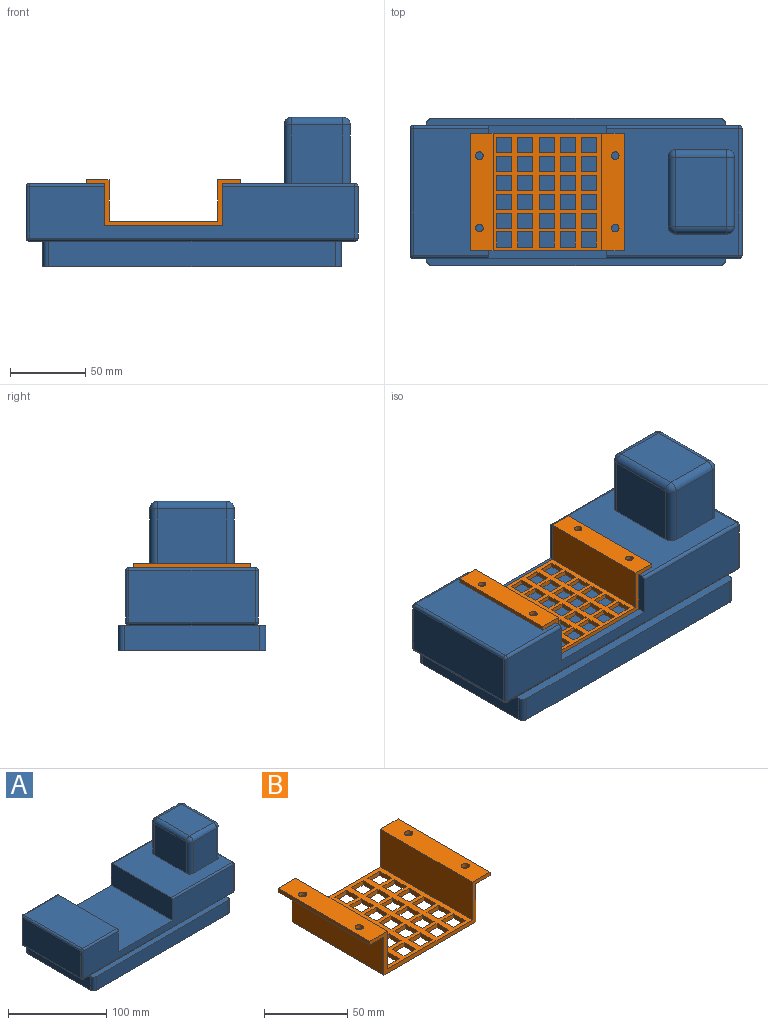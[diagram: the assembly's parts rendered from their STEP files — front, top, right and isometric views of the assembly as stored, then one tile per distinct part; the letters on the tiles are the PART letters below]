
ASSEMBLY  parts=2 mates=1
PART A: 61 faces, bbox 220x98x99 mm
  f0: plane 198x7mm, normal (0,0,1), area 1379.1mm2, adj f2,f3,f4,f7,f8,f37
  f1: plane 198x7mm, normal (0,0,1), area 1379.1mm2, adj f2,f4,f5,f9,f10,f29
  f2: plane 90x17mm, normal (-1,0,0), area 1530mm2, adj f0,f1,f6,f7,f10,f11
  f3: plane 190x17mm, normal (0,-1,0), area 3230mm2, adj f0,f6,f7,f8
  f4: plane 90x17mm, normal (1,0,0), area 1530mm2, adj f0,f1,f6,f8,f9,f18
  f5: plane 190x17mm, normal (0,1,0), area 3230mm2, adj f1,f6,f9,f10
  f6: plane 198x98mm, normal (0,0,-1), area 19390.3mm2, adj f2,f3,f4,f5,f7,f8,f9,f10
  f7: cylinder r=4mm len=17mm, axis (0,0,-1), area 106.8mm2, adj f0,f2,f3,f6
  f8: cylinder r=4mm len=17mm, axis (0,0,1), area 106.8mm2, adj f0,f3,f4,f6
  f9: cylinder r=4mm len=17mm, axis (0,0,-1), area 106.8mm2, adj f1,f4,f5,f6
  f10: cylinder r=4mm len=17mm, axis (0,0,1), area 106.8mm2, adj f1,f2,f5,f6
  f11: plane 84x9mm, normal (0,0,-1), area 756mm2, adj f2,f29,f30,f37
  f12: plane 88x84mm, normal (0,0,1), area 4949.5mm2, adj f19,f34,f40,f43,f44,f45,f46,f47
  f13: plane 216x34mm, normal (0,-1,0), area 5316mm2, adj f19,f20,f21,f26,f31,f37,f41,f43
  f14: plane 216x34mm, normal (0,1,0), area 5316mm2, adj f19,f20,f21,f22,f24,f29,f34,f35
  f15: plane 84x34mm, normal (-1,0,0), area 2856mm2, adj f24,f25,f30,f31
  f16: plane 84x34mm, normal (1,0,0), area 2856mm2, adj f35,f36,f40,f41
  f17: plane 84x50mm, normal (0,0,1), area 4200mm2, adj f20,f22,f25,f26
  f18: plane 84x9mm, normal (0,0,-1), area 756mm2, adj f4,f29,f36,f37
  f19: plane 88x28mm, normal (-1,0,0), area 2462.3mm2, adj f12,f13,f14,f21,f34,f43
  f20: plane 88x28mm, normal (1,0,0), area 2462.3mm2, adj f13,f14,f17,f21,f22,f26
  f21: plane 88x78mm, normal (0,0,1), area 6864mm2, adj f13,f14,f19,f20
  f22: cylinder r=2mm len=50mm, axis (1,0,0), area 157.1mm2, adj f14,f17,f20,f23
  f23: sphere r=2mm, area 6.3mm2, adj f22,f24,f25
  f24: cylinder r=2mm len=34mm, axis (0,0,1), area 106.8mm2, adj f14,f15,f23,f27
  f25: cylinder r=2mm len=84mm, axis (0,1,0), area 263.9mm2, adj f15,f17,f23,f28
  f26: cylinder r=2mm len=50mm, axis (-1,0,0), area 157.1mm2, adj f13,f17,f20,f28
  f27: sphere r=2mm, area 6.3mm2, adj f24,f29,f30
  f28: sphere r=2mm, area 6.3mm2, adj f25,f26,f31
  f29: cylinder r=2mm len=216mm, axis (-1,0,0), area 678.6mm2, adj f1,f11,f14,f18,f27,f32
  f30: cylinder r=2mm len=84mm, axis (0,-1,0), area 263.9mm2, adj f11,f15,f27,f33
  f31: cylinder r=2mm len=34mm, axis (0,0,-1), area 106.8mm2, adj f13,f15,f28,f33
  f32: sphere r=2mm, area 6.3mm2, adj f29,f35,f36
  f33: sphere r=2mm, area 6.3mm2, adj f30,f31,f37
  f34: cylinder r=2mm len=88mm, axis (1,0,0), area 276.5mm2, adj f12,f14,f19,f38
  f35: cylinder r=2mm len=34mm, axis (0,0,-1), area 106.8mm2, adj f14,f16,f32,f38
  f36: cylinder r=2mm len=84mm, axis (0,1,0), area 263.9mm2, adj f16,f18,f32,f39
  f37: cylinder r=2mm len=216mm, axis (1,0,0), area 678.6mm2, adj f0,f11,f13,f18,f33,f39
  f38: sphere r=2mm, area 6.3mm2, adj f34,f35,f40
  f39: sphere r=2mm, area 6.3mm2, adj f36,f37,f41
  f40: cylinder r=2mm len=84mm, axis (0,-1,0), area 263.9mm2, adj f12,f16,f38,f42
  f41: cylinder r=2mm len=34mm, axis (0,0,1), area 106.8mm2, adj f13,f16,f39,f42
  f42: sphere r=2mm, area 6.3mm2, adj f40,f41,f43
  f43: cylinder r=2mm len=88mm, axis (-1,0,0), area 276.5mm2, adj f12,f13,f19,f42
  f44: plane 39x34mm, normal (0,-1,0), area 1326mm2, adj f12,f51,f57,f60
  f45: plane 46x39mm, normal (1,0,0), area 1794mm2, adj f12,f54,f58,f60
  f46: plane 39x34mm, normal (0,1,0), area 1326mm2, adj f12,f49,f53,f54
  f47: plane 46x39mm, normal (-1,0,0), area 1794mm2, adj f12,f49,f51,f52
  f48: plane 46x34mm, normal (0,0,1), area 1564mm2, adj f52,f53,f57,f58
  f49: cylinder r=5mm len=39mm, axis (0,0,-1), area 306.3mm2, adj f12,f46,f47,f50
  f50: sphere r=5mm, area 39.3mm2, adj f49,f52,f53
  f51: cylinder r=5mm len=39mm, axis (0,0,1), area 306.3mm2, adj f12,f44,f47,f55
  f52: cylinder r=5mm len=46mm, axis (0,1,0), area 361.3mm2, adj f47,f48,f50,f55
  f53: cylinder r=5mm len=34mm, axis (1,0,0), area 267mm2, adj f46,f48,f50,f56
  f54: cylinder r=5mm len=39mm, axis (0,0,1), area 306.3mm2, adj f12,f45,f46,f56
  f55: sphere r=5mm, area 39.3mm2, adj f51,f52,f57
  f56: sphere r=5mm, area 39.3mm2, adj f53,f54,f58
  f57: cylinder r=5mm len=34mm, axis (-1,0,0), area 267mm2, adj f44,f48,f55,f59
  f58: cylinder r=5mm len=46mm, axis (0,-1,0), area 361.3mm2, adj f45,f48,f56,f59
  f59: sphere r=5mm, area 39.3mm2, adj f57,f58,f60
  f60: cylinder r=5mm len=39mm, axis (0,0,-1), area 306.3mm2, adj f12,f44,f45,f59
PART B: 138 faces, bbox 102x78x30.7 mm
  f0: plane 78x27.75mm, normal (-1,0,0), area 2164.4mm2, adj f1,f11,f12,f13
  f1: plane 78x72mm, normal (0,0,1), area 2615.8mm2, adj f0,f2,f12,f13,f18,f19,f20,f21
  f2: plane 78x27.75mm, normal (1,0,0), area 2164.4mm2, adj f1,f3,f12,f13
  f3: plane 78x15mm, normal (0,0,1), area 1130.7mm2, adj f2,f4,f12,f13,f16,f17
  f4: plane 78x2.75mm, normal (-1,0,0), area 214.4mm2, adj f3,f5,f12,f13
  f5: plane 78x12mm, normal (0,0,-1), area 896.6mm2, adj f4,f6,f12,f13,f16,f17
  f6: plane 78x28mm, normal (-1,0,0), area 2184mm2, adj f5,f7,f12,f13
  f7: plane 78x78mm, normal (0,0,-1), area 3084mm2, adj f6,f8,f12,f13,f18,f19,f20,f21
  f8: plane 78x28mm, normal (1,0,0), area 2184mm2, adj f7,f9,f12,f13
  f9: plane 78x12mm, normal (0,0,-1), area 896.6mm2, adj f8,f10,f12,f13,f14,f15
  f10: plane 78x2.75mm, normal (1,0,0), area 214.4mm2, adj f9,f11,f12,f13
  f11: plane 78x15mm, normal (0,0,1), area 1130.7mm2, adj f0,f10,f12,f13,f14,f15
  f12: plane 102x30.75mm, normal (0,-1,0), area 466.5mm2, adj f0,f1,f2,f3,f4,f5,f6,f7
  f13: plane 102x30.75mm, normal (0,1,0), area 466.5mm2, adj f0,f1,f2,f3,f4,f5,f6,f7
  f14: cylinder r=2.5mm len=5mm, axis (0,0,1), area 43.2mm2, adj f9,f11
  f15: cylinder r=2.5mm len=5mm, axis (0,0,1), area 43.2mm2, adj f9,f11
  f16: cylinder r=2.5mm len=5mm, axis (0,0,1), area 43.2mm2, adj f3,f5
  f17: cylinder r=2.5mm len=5mm, axis (0,0,1), area 43.2mm2, adj f3,f5
  f18: plane 10x3mm, normal (0,-1,0), area 30mm2, adj f1,f7,f19,f20
  f19: plane 10x3mm, normal (1,0,0), area 30mm2, adj f1,f7,f18,f21
  f20: plane 10x3mm, normal (-1,0,0), area 30mm2, adj f1,f7,f18,f21
  f21: plane 10x3mm, normal (0,1,0), area 30mm2, adj f1,f7,f19,f20
  f22: plane 10x3mm, normal (1,0,0), area 30mm2, adj f1,f7,f23,f24
  f23: plane 10x3mm, normal (0,1,0), area 30mm2, adj f1,f7,f22,f25
  f24: plane 10x3mm, normal (0,-1,0), area 30mm2, adj f1,f7,f22,f25
  f25: plane 10x3mm, normal (-1,0,0), area 30mm2, adj f1,f7,f23,f24
  f26: plane 10x3mm, normal (1,0,0), area 30mm2, adj f1,f7,f27,f28
  f27: plane 10x3mm, normal (0,1,0), area 30mm2, adj f1,f7,f26,f29
  f28: plane 10x3mm, normal (0,-1,0), area 30mm2, adj f1,f7,f26,f29
  f29: plane 10x3mm, normal (-1,0,0), area 30mm2, adj f1,f7,f27,f28
  f30: plane 10x3mm, normal (1,0,0), area 30mm2, adj f1,f7,f31,f32
  f31: plane 10x3mm, normal (0,1,0), area 30mm2, adj f1,f7,f30,f33
  f32: plane 10x3mm, normal (0,-1,0), area 30mm2, adj f1,f7,f30,f33
  f33: plane 10x3mm, normal (-1,0,0), area 30mm2, adj f1,f7,f31,f32
  f34: plane 10x3mm, normal (0,-1,0), area 30mm2, adj f1,f7,f35,f36
  f35: plane 10x3mm, normal (1,0,0), area 30mm2, adj f1,f7,f34,f37
  f36: plane 10x3mm, normal (-1,0,0), area 30mm2, adj f1,f7,f34,f37
  f37: plane 10x3mm, normal (0,1,0), area 30mm2, adj f1,f7,f35,f36
  f38: plane 10x3mm, normal (0,-1,0), area 30mm2, adj f1,f7,f39,f40
  f39: plane 10x3mm, normal (1,0,0), area 30mm2, adj f1,f7,f38,f41
  f40: plane 10x3mm, normal (-1,0,0), area 30mm2, adj f1,f7,f38,f41
  f41: plane 10x3mm, normal (0,1,0), area 30mm2, adj f1,f7,f39,f40
  f42: plane 10x3mm, normal (1,0,0), area 30mm2, adj f1,f7,f43,f44
  f43: plane 10x3mm, normal (0,1,0), area 30mm2, adj f1,f7,f42,f45
  f44: plane 10x3mm, normal (0,-1,0), area 30mm2, adj f1,f7,f42,f45
  f45: plane 10x3mm, normal (-1,0,0), area 30mm2, adj f1,f7,f43,f44
  f46: plane 10x3mm, normal (0,-1,0), area 30mm2, adj f1,f7,f47,f48
  f47: plane 10x3mm, normal (1,0,0), area 30mm2, adj f1,f7,f46,f49
  f48: plane 10x3mm, normal (-1,0,0), area 30mm2, adj f1,f7,f46,f49
  f49: plane 10x3mm, normal (0,1,0), area 30mm2, adj f1,f7,f47,f48
  f50: plane 10x3mm, normal (0,-1,0), area 30mm2, adj f1,f7,f51,f52
  f51: plane 10x3mm, normal (1,0,0), area 30mm2, adj f1,f7,f50,f53
  f52: plane 10x3mm, normal (-1,0,0), area 30mm2, adj f1,f7,f50,f53
  f53: plane 10x3mm, normal (0,1,0), area 30mm2, adj f1,f7,f51,f52
  f54: plane 10x3mm, normal (1,0,0), area 30mm2, adj f1,f7,f55,f56
  f55: plane 10x3mm, normal (0,1,0), area 30mm2, adj f1,f7,f54,f57
  f56: plane 10x3mm, normal (0,-1,0), area 30mm2, adj f1,f7,f54,f57
  f57: plane 10x3mm, normal (-1,0,0), area 30mm2, adj f1,f7,f55,f56
  f58: plane 10x3mm, normal (0,-1,0), area 30mm2, adj f1,f7,f59,f60
  f59: plane 10x3mm, normal (1,0,0), area 30mm2, adj f1,f7,f58,f61
  f60: plane 10x3mm, normal (-1,0,0), area 30mm2, adj f1,f7,f58,f61
  f61: plane 10x3mm, normal (0,1,0), area 30mm2, adj f1,f7,f59,f60
  f62: plane 10x3mm, normal (0,-1,0), area 30mm2, adj f1,f7,f63,f64
  f63: plane 10x3mm, normal (1,0,0), area 30mm2, adj f1,f7,f62,f65
  f64: plane 10x3mm, normal (-1,0,0), area 30mm2, adj f1,f7,f62,f65
  f65: plane 10x3mm, normal (0,1,0), area 30mm2, adj f1,f7,f63,f64
  f66: plane 10x3mm, normal (1,0,0), area 30mm2, adj f1,f7,f67,f68
  f67: plane 10x3mm, normal (0,1,0), area 30mm2, adj f1,f7,f66,f69
  f68: plane 10x3mm, normal (0,-1,0), area 30mm2, adj f1,f7,f66,f69
  f69: plane 10x3mm, normal (-1,0,0), area 30mm2, adj f1,f7,f67,f68
  f70: plane 10x3mm, normal (1,0,0), area 30mm2, adj f1,f7,f71,f72
  f71: plane 10x3mm, normal (0,1,0), area 30mm2, adj f1,f7,f70,f73
  f72: plane 10x3mm, normal (0,-1,0), area 30mm2, adj f1,f7,f70,f73
  f73: plane 10x3mm, normal (-1,0,0), area 30mm2, adj f1,f7,f71,f72
  f74: plane 10x3mm, normal (0,-1,0), area 30mm2, adj f1,f7,f75,f76
  f75: plane 10x3mm, normal (1,0,0), area 30mm2, adj f1,f7,f74,f77
  f76: plane 10x3mm, normal (-1,0,0), area 30mm2, adj f1,f7,f74,f77
  f77: plane 10x3mm, normal (0,1,0), area 30mm2, adj f1,f7,f75,f76
  f78: plane 10x3mm, normal (0,-1,0), area 30mm2, adj f1,f7,f79,f80
  f79: plane 10x3mm, normal (1,0,0), area 30mm2, adj f1,f7,f78,f81
  f80: plane 10x3mm, normal (-1,0,0), area 30mm2, adj f1,f7,f78,f81
  f81: plane 10x3mm, normal (0,1,0), area 30mm2, adj f1,f7,f79,f80
  f82: plane 10x3mm, normal (0,-1,0), area 30mm2, adj f1,f7,f83,f84
  f83: plane 10x3mm, normal (1,0,0), area 30mm2, adj f1,f7,f82,f85
  f84: plane 10x3mm, normal (-1,0,0), area 30mm2, adj f1,f7,f82,f85
  f85: plane 10x3mm, normal (0,1,0), area 30mm2, adj f1,f7,f83,f84
  f86: plane 10x3mm, normal (0,-1,0), area 30mm2, adj f1,f7,f87,f88
  f87: plane 10x3mm, normal (1,0,0), area 30mm2, adj f1,f7,f86,f89
  f88: plane 10x3mm, normal (-1,0,0), area 30mm2, adj f1,f7,f86,f89
  f89: plane 10x3mm, normal (0,1,0), area 30mm2, adj f1,f7,f87,f88
  f90: plane 10x3mm, normal (1,0,0), area 30mm2, adj f1,f7,f91,f92
  f91: plane 10x3mm, normal (0,1,0), area 30mm2, adj f1,f7,f90,f93
  f92: plane 10x3mm, normal (0,-1,0), area 30mm2, adj f1,f7,f90,f93
  f93: plane 10x3mm, normal (-1,0,0), area 30mm2, adj f1,f7,f91,f92
  f94: plane 10x3mm, normal (1,0,0), area 30mm2, adj f1,f7,f95,f96
  f95: plane 10x3mm, normal (0,1,0), area 30mm2, adj f1,f7,f94,f97
  f96: plane 10x3mm, normal (0,-1,0), area 30mm2, adj f1,f7,f94,f97
  f97: plane 10x3mm, normal (-1,0,0), area 30mm2, adj f1,f7,f95,f96
  f98: plane 10x3mm, normal (1,0,0), area 30mm2, adj f1,f7,f99,f100
  f99: plane 10x3mm, normal (0,1,0), area 30mm2, adj f1,f7,f98,f101
  f100: plane 10x3mm, normal (0,-1,0), area 30mm2, adj f1,f7,f98,f101
  f101: plane 10x3mm, normal (-1,0,0), area 30mm2, adj f1,f7,f99,f100
  f102: plane 10x3mm, normal (0,-1,0), area 30mm2, adj f1,f7,f103,f104
  f103: plane 10x3mm, normal (1,0,0), area 30mm2, adj f1,f7,f102,f105
  f104: plane 10x3mm, normal (-1,0,0), area 30mm2, adj f1,f7,f102,f105
  f105: plane 10x3mm, normal (0,1,0), area 30mm2, adj f1,f7,f103,f104
  f106: plane 10x3mm, normal (1,0,0), area 30mm2, adj f1,f7,f107,f108
  f107: plane 10x3mm, normal (0,1,0), area 30mm2, adj f1,f7,f106,f109
  f108: plane 10x3mm, normal (0,-1,0), area 30mm2, adj f1,f7,f106,f109
  f109: plane 10x3mm, normal (-1,0,0), area 30mm2, adj f1,f7,f107,f108
  f110: plane 10x3mm, normal (1,0,0), area 30mm2, adj f1,f7,f111,f112
  f111: plane 10x3mm, normal (0,1,0), area 30mm2, adj f1,f7,f110,f113
  f112: plane 10x3mm, normal (0,-1,0), area 30mm2, adj f1,f7,f110,f113
  f113: plane 10x3mm, normal (-1,0,0), area 30mm2, adj f1,f7,f111,f112
  f114: plane 10x3mm, normal (0,-1,0), area 30mm2, adj f1,f7,f115,f116
  f115: plane 10x3mm, normal (1,0,0), area 30mm2, adj f1,f7,f114,f117
  f116: plane 10x3mm, normal (-1,0,0), area 30mm2, adj f1,f7,f114,f117
  f117: plane 10x3mm, normal (0,1,0), area 30mm2, adj f1,f7,f115,f116
  f118: plane 10x3mm, normal (0,-1,0), area 30mm2, adj f1,f7,f119,f120
  f119: plane 10x3mm, normal (1,0,0), area 30mm2, adj f1,f7,f118,f121
  f120: plane 10x3mm, normal (-1,0,0), area 30mm2, adj f1,f7,f118,f121
  f121: plane 10x3mm, normal (0,1,0), area 30mm2, adj f1,f7,f119,f120
  f122: plane 10x3mm, normal (0,-1,0), area 30mm2, adj f1,f7,f123,f124
  f123: plane 10x3mm, normal (1,0,0), area 30mm2, adj f1,f7,f122,f125
  f124: plane 10x3mm, normal (-1,0,0), area 30mm2, adj f1,f7,f122,f125
  f125: plane 10x3mm, normal (0,1,0), area 30mm2, adj f1,f7,f123,f124
  f126: plane 10x3mm, normal (1,0,0), area 30mm2, adj f1,f7,f127,f128
  f127: plane 10x3mm, normal (0,1,0), area 30mm2, adj f1,f7,f126,f129
  f128: plane 10x3mm, normal (0,-1,0), area 30mm2, adj f1,f7,f126,f129
  f129: plane 10x3mm, normal (-1,0,0), area 30mm2, adj f1,f7,f127,f128
  f130: plane 10x3mm, normal (1,0,0), area 30mm2, adj f1,f7,f131,f132
  f131: plane 10x3mm, normal (0,1,0), area 30mm2, adj f1,f7,f130,f133
  f132: plane 10x3mm, normal (0,-1,0), area 30mm2, adj f1,f7,f130,f133
  f133: plane 10x3mm, normal (-1,0,0), area 30mm2, adj f1,f7,f131,f132
  f134: plane 10x3mm, normal (1,0,0), area 30mm2, adj f1,f7,f135,f136
  f135: plane 10x3mm, normal (0,1,0), area 30mm2, adj f1,f7,f134,f137
  f136: plane 10x3mm, normal (0,-1,0), area 30mm2, adj f1,f7,f134,f137
  f137: plane 10x3mm, normal (-1,0,0), area 30mm2, adj f1,f7,f135,f136
PLACE A t=(0,0,0.25)mm
PLACE B t=(-6.02,-4.81,36.88)mm
MATE fastened B.f7 <-> A.f21  axis (0,0,1) through (-8.99,-4.81,27.25)mm
